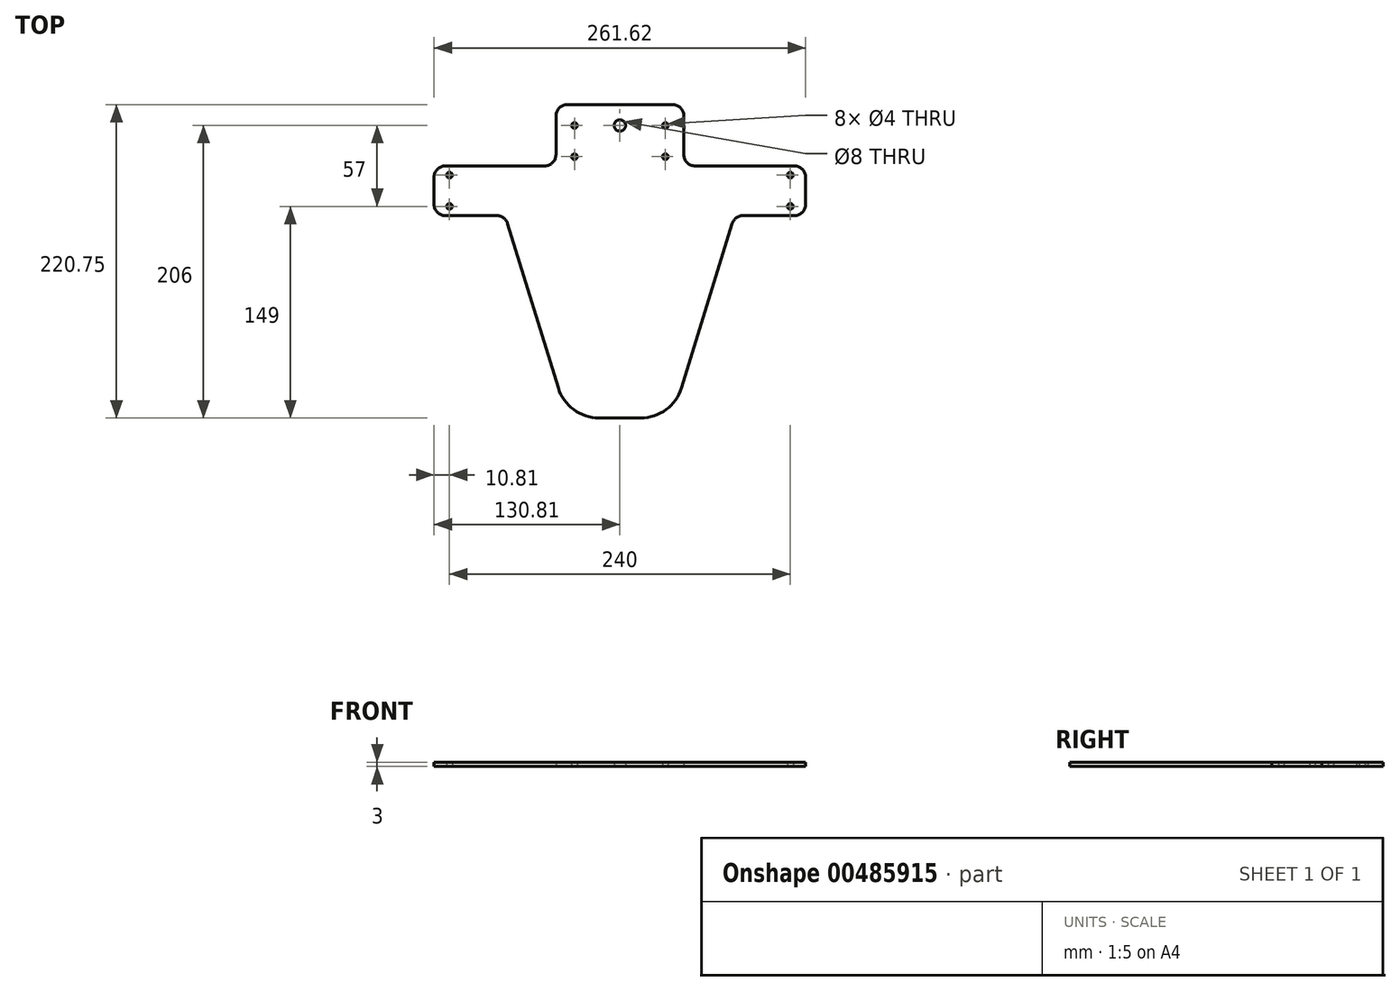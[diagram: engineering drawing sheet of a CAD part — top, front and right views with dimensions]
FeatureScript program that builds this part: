
annotation { "Feature Type Name" : "Feature", "Feature Type Description" : "" }
export const myFeature = defineFeature(function(context is Context, id is Id, definition is map)
    precondition{}
    {
        {
            var Q0;
            Q0=qCreatedBy(makeId("Top.planeOp"),FACE);
            var sketch = newSketch(context, id + "F0", { "sketchPlane" : qUnion([Q0])});
            skPoint(sketch, "E0", {"position": v(-120, 0) * mm});
            skPoint(sketch, "E1", {"position": v(120, 0) * mm});
            skPoint(sketch, "E2", {"position": v(-120, 11) * mm});
            skPoint(sketch, "E3", {"position": v(-120, -11) * mm});
            skPoint(sketch, "E4", {"position": v(120, 11) * mm});
            skPoint(sketch, "E5", {"position": v(120, -11) * mm});
            skPoint(sketch, "E6", {"position": v(0, 46) * mm});
            skPoint(sketch, "E7", {"position": v(32, 46) * mm});
            skPoint(sketch, "E8", {"position": v(-32, 46) * mm});
            skPoint(sketch, "E9", {"position": v(-32, 24) * mm});
            skPoint(sketch, "E10", {"position": v(32, 24) * mm});
            skLineSegment(sketch, "E11", {"start": v(-120, 11) * mm, "end": v(-120, 0) * mm});
            skLineSegment(sketch, "E12", {"start": v(-120, 0) * mm, "end": v(-120, -11) * mm});
            skLineSegment(sketch, "E13", {"start": v(-32, 46) * mm, "end": v(0, 46) * mm});
            skLineSegment(sketch, "E14", {"start": v(0, 46) * mm, "end": v(32, 46) * mm});
            skCircle(sketch, "E15", {"center": v(-120, -11) * mm, "radius": 2 * mm});
            skCircle(sketch, "E16", {"center": v(-120, 11) * mm, "radius": 2 * mm});
            skCircle(sketch, "E17", {"center": v(120, 11) * mm, "radius": 2 * mm});
            skCircle(sketch, "E18", {"center": v(120, -11) * mm, "radius": 2 * mm});
            skCircle(sketch, "E19", {"center": v(32, 24) * mm, "radius": 2 * mm});
            skCircle(sketch, "E20", {"center": v(32, 46) * mm, "radius": 2 * mm});
            skCircle(sketch, "E21", {"center": v(-32, 46) * mm, "radius": 2 * mm});
            skCircle(sketch, "E22", {"center": v(-32, 24) * mm, "radius": 2 * mm});
            skCircle(sketch, "E23", {"center": v(0, 46) * mm, "radius": 4 * mm});
            skLineSegment(sketch, "E24", {"start": v(0, 0) * mm, "end": v(-130.8, 0) * mm});
            skLineSegment(sketch, "E25", {"start": v(0, 0) * mm, "end": v(130.8, 0) * mm});
            skLineSegment(sketch, "E26", {"start": v(0, 0) * mm, "end": v(0, 60.75) * mm});
            skLineSegment(sketch, "E27", {"start": v(0, 0) * mm, "end": v(0, -160) * mm});
            skLineSegment(sketch, "E28", {"start": v(-130.8, 9.5) * mm, "end": v(-130.8, -9.5) * mm});
            skLineSegment(sketch, "E29", {"start": v(130.8, 9.5) * mm, "end": v(130.8, -9.5) * mm});
            skLineSegment(sketch, "E30", {"start": v(32.5, 60.75) * mm, "end": v(-32.5, 60.75) * mm});
            skPoint(sketch, "E31", {"position": v(-45, 17.5) * mm});
            skPoint(sketch, "E32", {"position": v(45, 17.5) * mm});
            skPoint(sketch, "E33", {"position": v(-80.8, -17.5) * mm});
            skPoint(sketch, "E34", {"position": v(130.8, -17.5) * mm});
            skPoint(sketch, "E35", {"position": v(80.8, -17.5) * mm});
            skLineSegment(sketch, "E36", {"start": v(-122.8, 17.5) * mm, "end": v(-53, 17.5) * mm});
            skLineSegment(sketch, "E37", {"start": v(-45, 52.75) * mm, "end": v(-45, 25.5) * mm});
            skLineSegment(sketch, "E38", {"start": v(-37, 60.75) * mm, "end": v(37, 60.75) * mm});
            skLineSegment(sketch, "E39", {"start": v(45, 52.75) * mm, "end": v(45, 25.5) * mm});
            skLineSegment(sketch, "E40", {"start": v(53, 17.5) * mm, "end": v(122.8, 17.5) * mm});
            skLineSegment(sketch, "E41", {"start": v(-122.8, -17.5) * mm, "end": v(-86.71, -17.5) * mm});
            skLineSegment(sketch, "E42", {"start": v(122.8, -17.5) * mm, "end": v(86.71, -17.5) * mm});
            skPoint(sketch, "E43.visualSharp", {"position": v(-130.8, 17.5) * mm});
            skArc(sketch, "E43.filletArc", {"start": v(-122.8, 17.5) * mm, "mid": v(-128.46, 15.16) * mm, "end": v(-130.8, 9.5) * mm});
            skPoint(sketch, "E44.visualSharp", {"position": v(-130.8, -17.5) * mm});
            skArc(sketch, "E44.filletArc", {"start": v(-130.8, -9.5) * mm, "mid": v(-128.46, -15.16) * mm, "end": v(-122.8, -17.5) * mm});
            skPoint(sketch, "E45.visualSharp", {"position": v(130.8, 17.5) * mm});
            skArc(sketch, "E45.filletArc", {"start": v(130.8, 9.5) * mm, "mid": v(128.46, 15.16) * mm, "end": v(122.8, 17.5) * mm});
            skArc(sketch, "E46.filletArc", {"start": v(122.8, -17.5) * mm, "mid": v(128.46, -15.16) * mm, "end": v(130.8, -9.5) * mm});
            skPoint(sketch, "E47.visualSharp", {"position": v(45, 60.75) * mm});
            skArc(sketch, "E47.filletArc", {"start": v(45, 52.75) * mm, "mid": v(42.66, 58.4) * mm, "end": v(37, 60.75) * mm});
            skPoint(sketch, "E48.visualSharp", {"position": v(-45, 60.75) * mm});
            skArc(sketch, "E48.filletArc", {"start": v(-37, 60.75) * mm, "mid": v(-42.66, 58.4) * mm, "end": v(-45, 52.75) * mm});
            skArc(sketch, "E49.filletArc", {"start": v(45, 25.5) * mm, "mid": v(47.34, 19.84) * mm, "end": v(53, 17.5) * mm});
            skArc(sketch, "E50.filletArc", {"start": v(-53, 17.5) * mm, "mid": v(-47.34, 19.84) * mm, "end": v(-45, 25.5) * mm});
            skLineSegment(sketch, "E51", {"start": v(-14.74, -160) * mm, "end": v(0, -160) * mm});
            skLineSegment(sketch, "E52", {"start": v(0, -160) * mm, "end": v(14.74, -160) * mm});
            skLineSegment(sketch, "E53", {"start": v(-79.07, -23.14) * mm, "end": v(-43.4, -138.84) * mm});
            skLineSegment(sketch, "E54", {"start": v(43.4, -138.84) * mm, "end": v(79.07, -23.14) * mm});
            skArc(sketch, "E55.filletArc", {"start": v(-79.07, -23.14) * mm, "mid": v(-81.96, -19.06) * mm, "end": v(-86.71, -17.5) * mm});
            skArc(sketch, "E56.filletArc", {"start": v(86.71, -17.5) * mm, "mid": v(81.96, -19.06) * mm, "end": v(79.07, -23.14) * mm});
            skPoint(sketch, "E57.visualSharp", {"position": v(36.88, -160) * mm});
            skArc(sketch, "E57.filletArc", {"start": v(14.74, -160) * mm, "mid": v(32.55, -154.14) * mm, "end": v(43.4, -138.84) * mm});
            skPoint(sketch, "E58.visualSharp", {"position": v(-36.88, -160) * mm});
            skArc(sketch, "E58.filletArc", {"start": v(-43.4, -138.84) * mm, "mid": v(-32.55, -154.14) * mm, "end": v(-14.74, -160) * mm});
            skSolve(sketch);
        }
        {
            var Q0;
            Q0=makeQuery(id+"F0.imprint","IMPRINT",FACE,{"disambiguationData":[TD([[makeQuery(id+"F0.imprint","IMPRINT",EDGE,{"derivedFrom":sQuery(id+"F0.wireOp",EDGE,"E16")}),-1.0]])]});
            var Q1;
            Q1=makeQuery(id+"F0.imprint","IMPRINT",FACE,{"disambiguationData":[TD([[makeQuery(id+"F0.imprint","IMPRINT",EDGE,{"derivedFrom":sQuery(id+"F0.wireOp",EDGE,"E17")}),-1.0]])]});
            var Q2;
            Q2=makeQuery(id+"F0.imprint","IMPRINT",FACE,{"disambiguationData":[TD([[makeQuery(id+"F0.imprint","IMPRINT",EDGE,{"derivedFrom":sQuery(id+"F0.wireOp",EDGE,"E18")}),-1.0]])]});
            var Q3;
            Q3=makeQuery(id+"F0.imprint","IMPRINT",FACE,{"disambiguationData":[TD([[makeQuery(id+"F0.imprint","IMPRINT",EDGE,{"derivedFrom":sQuery(id+"F0.wireOp",EDGE,"E15")}),-1.0]])]});
            extrude(context, id + "F1", {"entities" : qUnion([Q0, Q1, Q2, Q3]), "depth" : 3 * mm});
        }
    });
